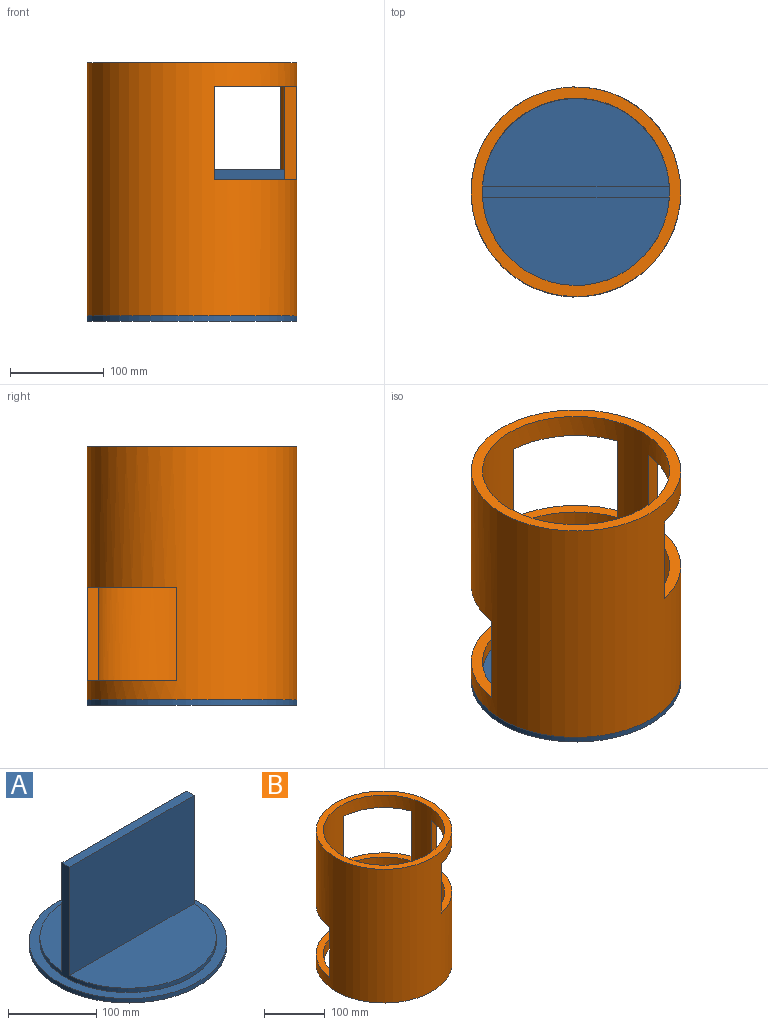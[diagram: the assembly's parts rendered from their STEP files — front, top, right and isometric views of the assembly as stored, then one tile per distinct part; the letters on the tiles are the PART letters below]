
ASSEMBLY  parts=2 mates=1
PART A: 9 faces, bbox 224x224x162 mm
  f0: plane 199.64x94mm, normal (0,0,1), area 14508.7mm2, adj f4,f7
  f1: cylinder r=112mm len=224mm, axis (0,0,-1), area 4222.3mm2, adj f2,f3
  f2: plane 224x224mm, normal (0,0,1), area 7992.2mm2, adj f1,f4
  f3: plane 224x224mm, normal (0,0,-1), area 39408.1mm2, adj f1
  f4: cylinder r=100mm len=200mm, axis (0,0,-1), area 7372.1mm2, adj f0,f2,f5,f6,f7,f8
  f5: plane 199.64x94mm, normal (0,0,1), area 14508.7mm2, adj f4,f6
  f6: plane 199.64x150mm, normal (0,-1,0), area 29946mm2, adj f4,f5,f8
  f7: plane 199.64x150mm, normal (0,1,0), area 29946mm2, adj f0,f4,f8
  f8: plane 200x12mm, normal (0,0,1), area 2398.6mm2, adj f4,f6,f7
PART B: 16 faces, bbox 224x224x270 mm
  f0: plane 98.65x89.48mm, normal (0,0,1), area 1581.9mm2, adj f2,f3,f10,f12
  f1: plane 100.55x79.97mm, normal (0,0,1), area 1514.2mm2, adj f2,f3,f9,f11
  f2: cylinder r=100mm len=270mm, axis (0,0,-1), area 131359.1mm2, adj f0,f1,f4,f5,f6,f7,f8,f9
  f3: cylinder r=112mm len=270mm, axis (0,0,-1), area 147122.2mm2, adj f0,f1,f4,f5,f6,f7,f8,f9
  f4: plane 107.83x97.35mm, normal (0,0,1), area 1773.9mm2, adj f2,f3,f6,f7
  f5: plane 224x224mm, normal (0,0,-1), area 7992.2mm2, adj f2,f3
  f6: plane 100x11.99mm, normal (-1,-0.03,0), area 1200mm2, adj f2,f3,f4,f8
  f7: plane 100x11.87mm, normal (0.15,0.99,0), area 1200mm2, adj f2,f3,f4,f8
  f8: plane 107.83x97.35mm, normal (0,0,-1), area 1773.9mm2, adj f2,f3,f6,f7
  f9: plane 100x11.98mm, normal (1,-0.06,0), area 1200mm2, adj f1,f2,f3,f13
  f10: plane 100x11.71mm, normal (0.98,0.22,0), area 1200mm2, adj f0,f2,f3,f14
  f11: plane 100x11.38mm, normal (-0.32,0.95,0), area 1200mm2, adj f1,f2,f3,f13
  f12: plane 100x11.93mm, normal (-0.11,-0.99,0), area 1200mm2, adj f0,f2,f3,f14
  f13: plane 100.55x79.97mm, normal (0,0,-1), area 1514.2mm2, adj f2,f3,f9,f11
  f14: plane 98.65x89.48mm, normal (0,0,-1), area 1581.9mm2, adj f2,f3,f10,f12
  f15: plane 224x224mm, normal (0,0,1), area 7992.2mm2, adj f2,f3
PLACE A t=(-84.09,-3.37,-14.56)mm
PLACE B t=(-84.09,-3.37,-8.56)mm
MATE planar B.f2 <-> A.f1  axis (0,0,-1) through (-84.09,-3.37,-8.56)mm
